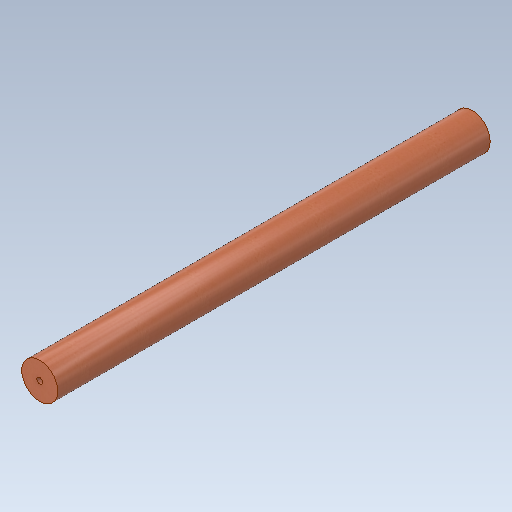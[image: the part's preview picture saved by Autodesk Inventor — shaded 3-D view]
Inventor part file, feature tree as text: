
AUTODESK INVENTOR PART (.ipt)
format: ipt  version: 2020.1 (Build 241239000, 239)  size: 127,488 bytes
history: native  units: in
note: dims shown in document units (in); Inventor stores cm internally (conversion verified against a paired STEP export)
features: sketch x2, extrude x1, hole x1
ambient origin geometry x8: Origin, YZ Plane, XZ Plane, XY Plane, X Axis, Y Axis, Z Axis, Center Point
bodies: Solid1 (feature_tree)
feature tree (4):
  extrude  "Extrusion1"  Depth=72.0in TaperAngle=0.0deg
  hole  "Hole1"  [1 undecoded]
  sketch  "Sketch1"  dims[d0=6.0in d1=72.0in d2=0.0in]
  sketch  "Sketch2"  dims[d3=1.0in d4=0.75in d5=0.375in d6=0.25in d7=0.5635in d8=1.0in d9=0.8108in]
note: 1 required parameter value undecoded (feature->parameter linkage not recoverable at this tier; creation-order binding heuristic only, values carry confidence <= 0.55)
